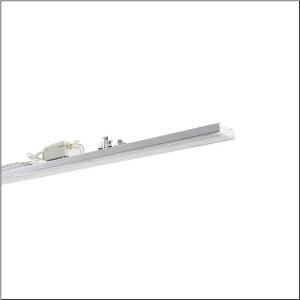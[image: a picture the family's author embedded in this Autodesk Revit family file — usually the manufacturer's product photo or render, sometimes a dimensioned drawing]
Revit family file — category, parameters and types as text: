
# Revit family: licross_r__21_recessed_mo_52tl187n485g_8ad4
name_source: partatom
category: Lighting Fixtures
units: mm (PartAtom-declared; Revit-internal decimal feet)

## family parameters
Cut with Voids When Loaded = No
Host = Face
Light Source = No
Part Type = Normal
Room Calculation Point = No
Round Connector Dimension = Use Diameter
Shared = No

## types (1)
- Licross® 21 Recessed MO (1 x LED, 8570 lm, 47.9 W, 4000K)
    Apparent Load = 48 VA
    CIE Flux Codes = 79 95 99 100 100
    Color Rendering = 80
    Color Temperature = 4000K
    Default Elevation = 1800 mm
    Description = Licross® 21 Recessed MO, luminaire insert, of sheet steel, galvanised, coil coated, white, length: 1.500mm, width: 66mm, height: 67mm, LED rated luminous flux: 8.570lm, light colour: 840, control gear: ON/OFF, with plug, 3-pole, with phase selection, mains connection: 220..240V, AC, 50/60Hz, rated input power: 48W, halogen-free wiring, primary light control with lens, of plastic, primary optical cover: cover, of PMMA, light emission: direct distribution, primary light characteristic: symmetric, protection rating (complete): IP40, insulation class (complete): insulation class I (protective earthing), certification: CE, ENEC, VDE, UKCA, protection symbol: D if used in an environment without relevant dust loads with corresponding accessories, impact resistance: IK06, permissible ambient temperature for indoor applications: -35..+40°C, corresponds to IFS (International Featured Standards) requirements for safety and quality in the food industry, reducing of maximum allowable ambient temperature of 5°C with ceiling mounting, LABS conformity tested according to VDMA 24364:2018-05, packaging unit: 1 piece
    Height = 58 mm
    Lamp = 1 x LED
    Lamp Light Flux = 8570 lm
    Lamp Power = 47.9 W
    Lamp count = 1
    Length = 1500 mm
    Luminous efficacy = 179 lm/W
    Manufacturer = Siteco
    ModVariant = No
    Model = 52TL187N485G
    Mounting Place = Ceiling
    Mounting Type = Pendant
    Number of Poles = 1
    OnlyDefault = Yes
    Power Factor = 1
    Product Name = Licross® 21 Recessed MO
    Product group = luminaire insert
    ProductGroupID = 901
    Protection Class = Protection class I
    Protection Degree = IP 40
    RLX_Detail_Level = 1
    RLX_Emergency_Light_Flux = 0 lm
    RLX_Emergency_Type = 0
    RLX_Emergency_Type_DB = No
    RlxData = <blob elided: 20853 chars, md5=b3cf180c>
    Socket = socket
    Standby Power = 0 W
    System Light Flux = 8570 lm
    System Power = 48 W
    Type Comments = Product without accessories
    Type Image = l_1296930.jpg
    URL = http://relux.com
    VarID = ---
    Voltage = 0 V
    Weight = 0.00 kg
    Width = 66 mm

## geometry (parser evidence)
native form markers: Blend x4, Sweep x10
no freeform markers — native parametric forms only
